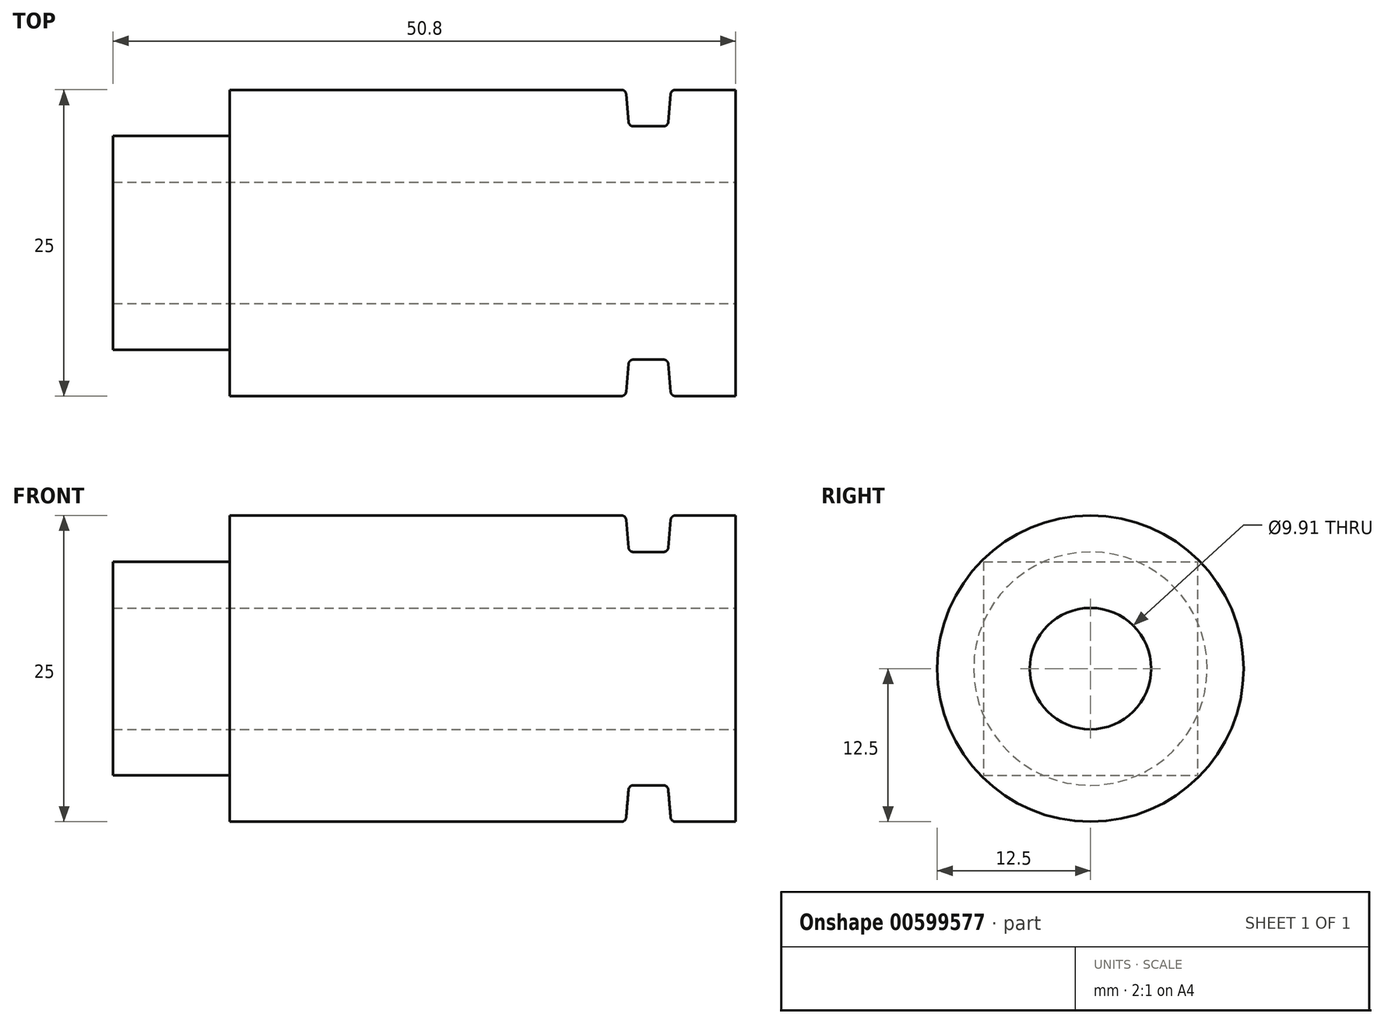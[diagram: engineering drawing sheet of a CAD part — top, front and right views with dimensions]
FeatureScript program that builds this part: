
annotation { "Feature Type Name" : "Feature", "Feature Type Description" : "" }
export const myFeature = defineFeature(function(context is Context, id is Id, definition is map)
    precondition{}
    {
        {
            var Q0;
            Q0=qCreatedBy(makeId("Front.planeOp"),FACE);
            var sketch = newSketch(context, id + "F0", { "sketchPlane" : qUnion([Q0])});
            skLineSegment(sketch, "E0", {"start": v(-20.64, 12.5) * mm, "end": v(11.32, 12.5) * mm});
            skLineSegment(sketch, "E1", {"start": v(11.7, 12.15) * mm, "end": v(11.9, 9.87) * mm});
            skLineSegment(sketch, "E2", {"start": v(12.27, 9.52) * mm, "end": v(14.75, 9.52) * mm});
            skLineSegment(sketch, "E3", {"start": v(15.13, 9.87) * mm, "end": v(15.33, 12.15) * mm});
            skLineSegment(sketch, "E4", {"start": v(15.7, 12.5) * mm, "end": v(20.64, 12.5) * mm});
            skLineSegment(sketch, "E5", {"start": v(20.64, 12.5) * mm, "end": v(20.64, 0) * mm});
            skLineSegment(sketch, "E6", {"start": v(11.93, 9.52) * mm, "end": v(11.93, 26.9) * mm, "construction": true});
            skLineSegment(sketch, "E7", {"start": v(15.1, 9.52) * mm, "end": v(15.1, 22.42) * mm, "construction": true});
            skPoint(sketch, "E8.visualSharp", {"position": v(11.93, 9.52) * mm});
            skArc(sketch, "E8.filletArc", {"start": v(11.9, 9.87) * mm, "mid": v(12.02, 9.63) * mm, "end": v(12.27, 9.52) * mm});
            skPoint(sketch, "E9.visualSharp", {"position": v(15.1, 9.52) * mm});
            skArc(sketch, "E9.filletArc", {"start": v(14.75, 9.52) * mm, "mid": v(15, 9.63) * mm, "end": v(15.13, 9.87) * mm});
            skPoint(sketch, "E10.visualSharp", {"position": v(11.67, 12.5) * mm});
            skArc(sketch, "E10.filletArc", {"start": v(11.7, 12.15) * mm, "mid": v(11.57, 12.4) * mm, "end": v(11.32, 12.5) * mm});
            skPoint(sketch, "E11.visualSharp", {"position": v(15.36, 12.5) * mm});
            skArc(sketch, "E11.filletArc", {"start": v(15.7, 12.5) * mm, "mid": v(15.45, 12.4) * mm, "end": v(15.33, 12.15) * mm});
            skLineSegment(sketch, "E12", {"start": v(0, 121.06) * mm, "end": v(0, -104.42) * mm, "construction": true});
            skLineSegment(sketch, "E13", {"start": v(-20.64, 12.5) * mm, "end": v(-20.64, 0) * mm});
            skLineSegment(sketch, "E14", {"start": v(-20.64, 0) * mm, "end": v(20.64, 0) * mm});
            skLineSegment(sketch, "E15", {"start": v(100.64, 0) * mm, "end": v(-105.06, 0) * mm, "construction": true});
            skSolve(sketch);
        }
        {
            var Q0;
            Q0=makeQuery(id+"F0.imprint","IMPRINT",FACE,{"disambiguationData":[TD([[makeQuery(id+"F0.imprint","IMPRINT",EDGE,{"derivedFrom":sQuery(id+"F0.wireOp",EDGE,"E0")}),-1.0]])]});
            var Q1;
            Q1=sQuery(id+"F0.wireOp",EDGE,"E15");
            revolve(context, id + "F1", {"surfaceOperationType" : NewSurfaceOperationType.NEW, "entities" : qUnion([Q0]), "axis" : qUnion([Q1]), "revolveType" : RevolveType.FULL});
        }
        {
            var Q0;
            Q0=makeQuery(id+"F1.opRevolve","SWEPT_FACE",FACE,{"disambiguationData":[OSD([sQuery(id+"F0.wireOp",EDGE,"E13")])]});
            var sketch = newSketch(context, id + "F2", { "sketchPlane" : qUnion([Q0])});
            skLineSegment(sketch, "E16.bottom", {"start": v(8.72, 8.72) * mm, "end": v(-8.72, 8.72) * mm});
            skLineSegment(sketch, "E16.top", {"start": v(8.72, -8.72) * mm, "end": v(-8.72, -8.72) * mm});
            skLineSegment(sketch, "E16.left", {"start": v(8.72, 8.72) * mm, "end": v(8.72, -8.72) * mm});
            skLineSegment(sketch, "E16.right", {"start": v(-8.72, 8.72) * mm, "end": v(-8.72, -8.72) * mm});
            skPoint(sketch, "E16.middle", {"position": v(0, 0) * mm});
            skSolve(sketch);
        }
        {
            var Q0;
            Q0 = qSketchRegion(id + "F2", true);
            extrude(context, id + "F3", {"entities" : qUnion([Q0]), "operationType" : NewBodyOperationType.ADD, "depth" : 9.52 * mm, "offsetDistance" : 25.4 * mm});
        }
        {
            var Q0;
            Q0=makeQuery(id+"F1.opRevolve","SWEPT_FACE",FACE,{"disambiguationData":[OSD([sQuery(id+"F0.wireOp",EDGE,"E5")])]});
            var sketch = newSketch(context, id + "F4", { "sketchPlane" : qUnion([Q0])});
            skCircle(sketch, "E17", {"center": v(0, 0) * mm, "radius": 4.95 * mm});
            skSolve(sketch);
        }
        {
            var Q0;
            Q0 = qSketchRegion(id + "F4", true);
            extrude(context, id + "F5", {"entities" : qUnion([Q0]), "operationType" : NewBodyOperationType.REMOVE, "endBound" : BoundingType.THROUGH_ALL, "oppositeDirection" : true, "depth" : 25.4 * mm, "offsetDistance" : 25.4 * mm});
        }
    });
